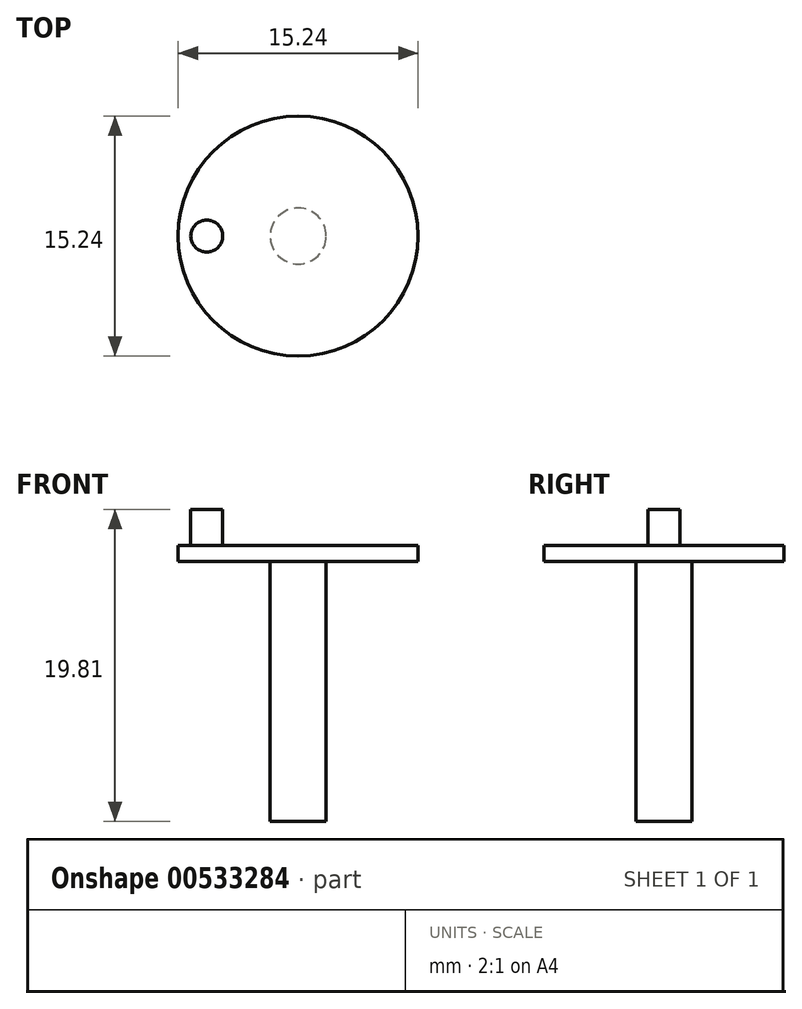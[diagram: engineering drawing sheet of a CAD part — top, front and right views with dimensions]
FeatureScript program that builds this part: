
annotation { "Feature Type Name" : "Feature", "Feature Type Description" : "" }
export const myFeature = defineFeature(function(context is Context, id is Id, definition is map)
    precondition{}
    {
        {
            var Q0;
            Q0=qCreatedBy(makeId("Top.planeOp"),FACE);
            var sketch = newSketch(context, id + "F0", { "sketchPlane" : qUnion([Q0])});
            skCircle(sketch, "E0", {"center": v(0, 0) * mm, "radius": 7.62 * mm});
            skSolve(sketch);
        }
        {
            var Q0;
            Q0=makeQuery(id+"F0.imprint","IMPRINT",FACE,{"disambiguationData":[TD([[makeQuery(id+"F0.imprint","IMPRINT",EDGE,{"derivedFrom":sQuery(id+"F0.wireOp",EDGE,"E0")}),1.0]])]});
            extrude(context, id + "F1", {"entities" : qUnion([Q0]), "depth" : 1.02 * mm, "offsetDistance" : 25.4 * mm});
        }
        {
            var Q0;
            Q0=makeQuery(id+"F1.opExtrude","CAP_FACE",FACE,{"disambiguationData":[OSD([sQuery(id+"F0.wireOp",EDGE,"E0")])],"isStart":false});
            var sketch = newSketch(context, id + "F2", { "sketchPlane" : qUnion([Q0])});
            skCircle(sketch, "E1", {"center": v(-5.8, 0) * mm, "radius": 1.02 * mm});
            skSolve(sketch);
        }
        {
            var Q0;
            Q0=makeQuery(id+"F2.imprint","IMPRINT",FACE,{"disambiguationData":[TD([[makeQuery(id+"F2.imprint","IMPRINT",EDGE,{"derivedFrom":sQuery(id+"F2.wireOp",EDGE,"E1")}),1.0]])]});
            extrude(context, id + "F3", {"entities" : qUnion([Q0]), "operationType" : NewBodyOperationType.ADD, "depth" : 2.3 * mm, "offsetDistance" : 25.4 * mm});
        }
        {
            var Q0;
            Q0=makeQuery(id+"F1.opExtrude","CAP_FACE",FACE,{"disambiguationData":[OSD([sQuery(id+"F0.wireOp",EDGE,"E0")])],"isStart":true});
            var sketch = newSketch(context, id + "F4", { "sketchPlane" : qUnion([Q0])});
            skCircle(sketch, "E2", {"center": v(0, 0) * mm, "radius": 1.78 * mm});
            skSolve(sketch);
        }
        {
            var Q0;
            Q0 = qSketchRegion(id + "F4", true);
            extrude(context, id + "F5", {"entities" : qUnion([Q0]), "operationType" : NewBodyOperationType.ADD, "depth" : 16.5 * mm, "offsetDistance" : 25.4 * mm});
        }
    });
